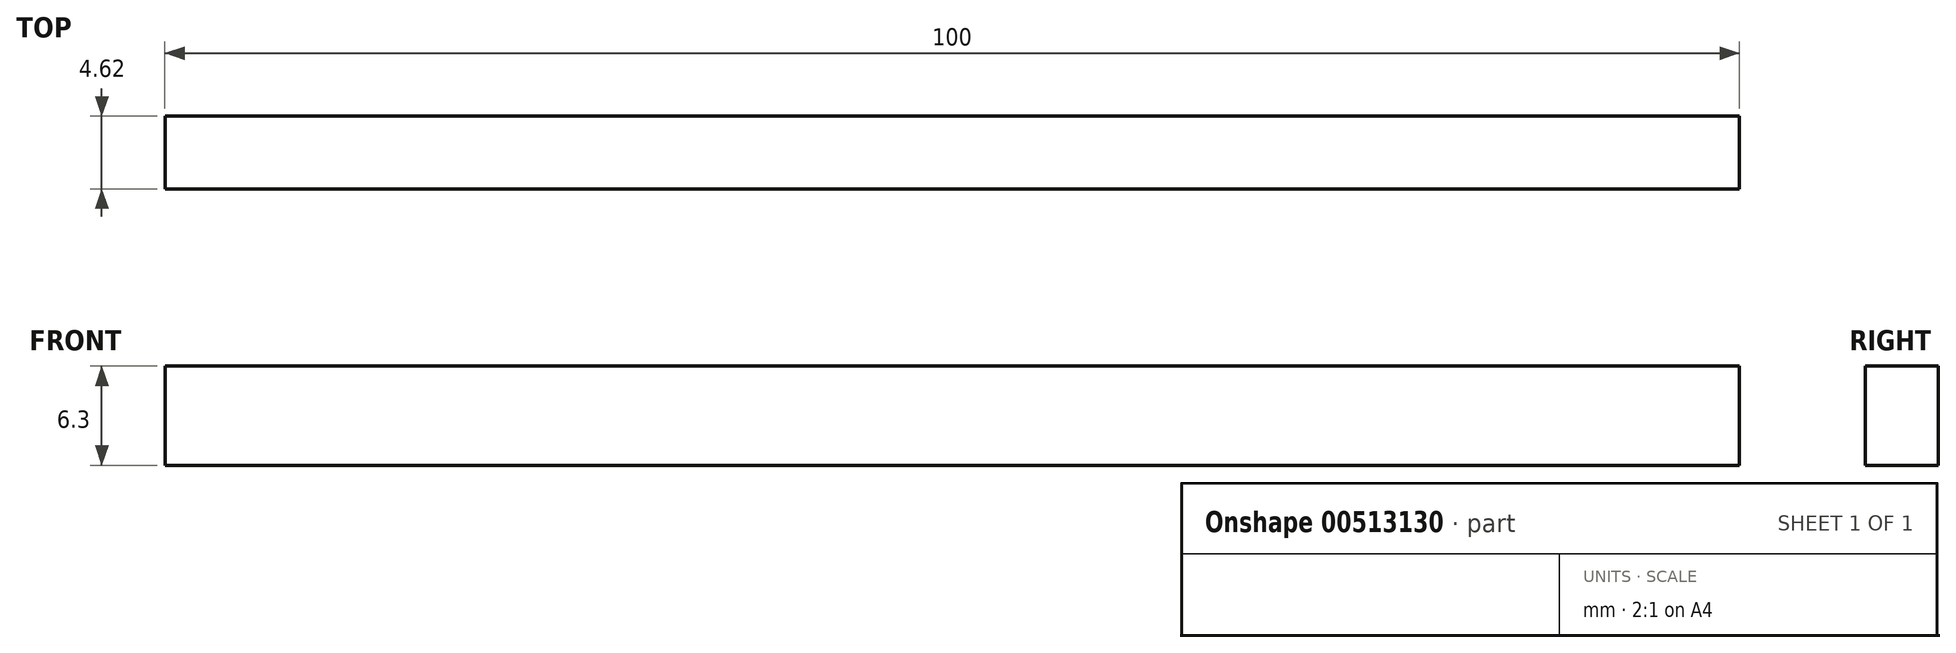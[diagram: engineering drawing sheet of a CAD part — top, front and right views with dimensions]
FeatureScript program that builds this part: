
annotation { "Feature Type Name" : "Feature", "Feature Type Description" : "" }
export const myFeature = defineFeature(function(context is Context, id is Id, definition is map)
    precondition{}
    {
        {
            var Q0;
            Q0=qCreatedBy(makeId("Front.planeOp"),FACE);
            var sketch = newSketch(context, id + "F0", { "sketchPlane" : qUnion([Q0])});
            skLineSegment(sketch, "E0.bottom", {"start": v(-79.64, 20.48) * mm, "end": v(20.36, 20.48) * mm});
            skLineSegment(sketch, "E0.top", {"start": v(-79.64, 14.18) * mm, "end": v(20.36, 14.18) * mm});
            skLineSegment(sketch, "E0.left", {"start": v(-79.64, 20.48) * mm, "end": v(-79.64, 14.18) * mm});
            skLineSegment(sketch, "E0.right", {"start": v(20.36, 20.48) * mm, "end": v(20.36, 14.18) * mm});
            skSolve(sketch);
        }
        {
            var Q0;
            Q0=makeQuery(id+"F0.imprint","IMPRINT",FACE,{"disambiguationData":[TD([[makeQuery(id+"F0.imprint","IMPRINT",EDGE,{"derivedFrom":sQuery(id+"F0.wireOp",EDGE,"E0.bottom")}),-1.0]])]});
            extrude(context, id + "F1", {"entities" : qUnion([Q0]), "depth" : 4.62 * mm});
        }
    });
